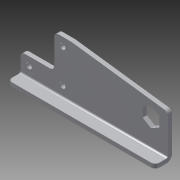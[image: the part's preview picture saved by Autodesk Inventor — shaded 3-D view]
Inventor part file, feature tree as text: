
AUTODESK INVENTOR PART (.ipt)
format: ipt  version: 2014 (Build 180170000, 170)  size: 199,168 bytes
history: native  units: in
note: dims shown in document units (in); Inventor stores cm internally (conversion verified against a paired STEP export)
features: sheet_metal_op x4, other x3, sketch x2, fillet x1, extrude x1
ambient origin geometry x8: Origin, YZ Plane, XZ Plane, XY Plane, X Axis, Y Axis, Z Axis, Center Point
bodies: Solid1 (feature_tree)
feature tree (11):
  sheet_metal_op  "Face1"
  sheet_metal_op  "Flange1"
  fillet  "Fillet2"  Radius=0.5in
  sketch  "Sketch1"  dims[d1=1.0in d2=1.0in]
  other  "Plate1"
  sketch  "Sketch2"  dims[d3=0.5in d4=4.375in d5=0.5in d6=0.75in d7=0.5in d8=90.0deg d9=1.125in d10=0.163in d11=0.25in d12=0.25in d13=0.7874in d15=1.0in d16=0.3937in d18=1.0in d20=0.7874in d22=1.0in d23=0.3937in d25=1.0in d27=0.125in d29=0.125in d30=0.0625in d31=0.25in d32=0.125in d33=0.5in d34=90.0deg d35=0.05in d36=0.5in d37=0.125in d38=0.125in d39=0.125in]
  other  "Plate2"
  sheet_metal_op  "Bend1"
  sheet_metal_op  "Corner1"
  other  "Definition1"
  extrude  "Extrusion1"  Depth=1.0in
